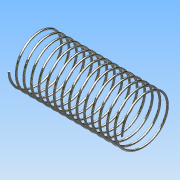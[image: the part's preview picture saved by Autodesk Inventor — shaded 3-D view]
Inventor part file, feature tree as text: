
AUTODESK INVENTOR PART (.ipt)
format: ipt  version: 2014 (Build 180170000, 170)  size: 401,920 bytes
history: native  units: in
note: dims shown in document units (in); Inventor stores cm internally (conversion verified against a paired STEP export)
features: sketch x2, extrude x1, helix x1
ambient origin geometry x8: Origin, YZ Plane, XZ Plane, XY Plane, X Axis, Y Axis, Z Axis, Center Point
bodies: Solid1 (feature_tree)
feature tree (4):
  extrude  "Extrusion1"  TaperAngle=0.0deg  [1 undecoded]
  helix  "Coil2"  [1 undecoded]
  sketch  "Sketch1"  dims[d0=0.67in d2=0.0in d12=0.025in]
  sketch  "Sketch3"  dims[d13=0.1in d14=1.5in d15=0.3937in d16=0.0in d17=90.0deg d18=90.0deg d19=0.0in d20=0.0in]
note: 2 required parameter values undecoded (feature->parameter linkage not recoverable at this tier; creation-order binding heuristic only, values carry confidence <= 0.55)
